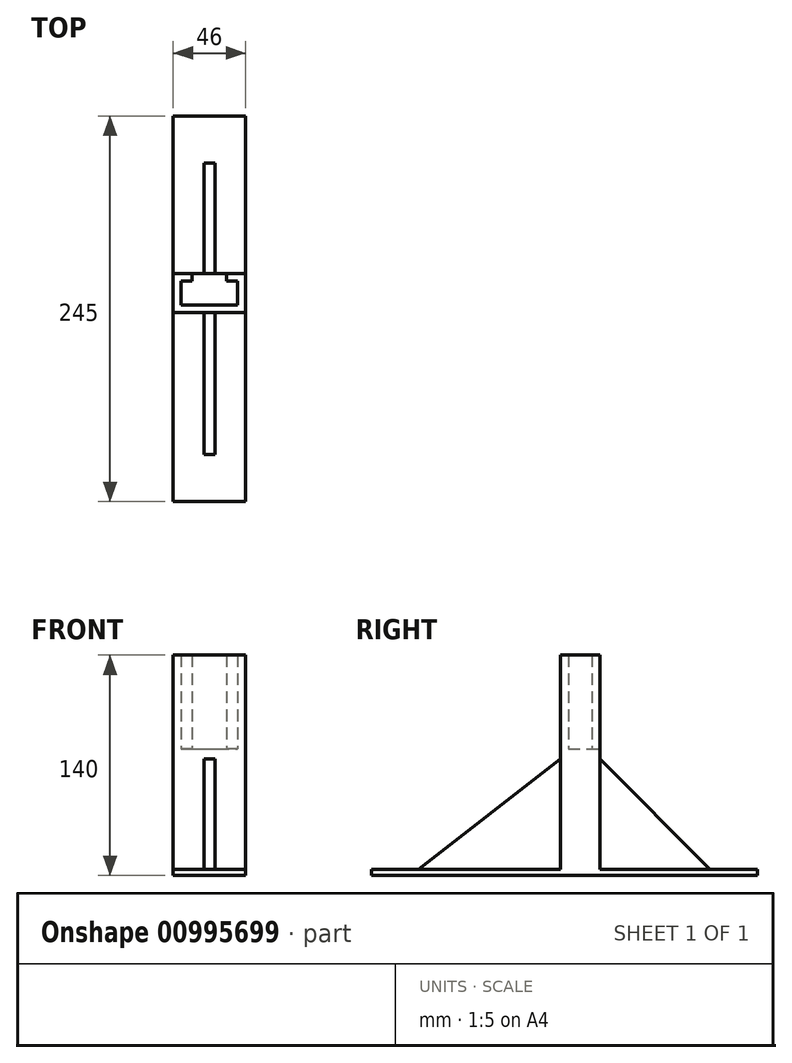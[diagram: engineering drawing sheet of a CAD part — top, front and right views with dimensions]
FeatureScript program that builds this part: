
annotation { "Feature Type Name" : "Feature", "Feature Type Description" : "" }
export const myFeature = defineFeature(function(context is Context, id is Id, definition is map)
    precondition{}
    {
        {
            var Q0;
            Q0=qCreatedBy(makeId("Front.planeOp"),FACE);
            var sketch = newSketch(context, id + "F0", { "sketchPlane" : qUnion([Q0])});
            skLineSegment(sketch, "E0.bottom", {"start": v(-35.47, 8.44) * mm, "end": v(10.53, 8.44) * mm});
            skLineSegment(sketch, "E0.top", {"start": v(-35.47, -71.56) * mm, "end": v(10.53, -71.56) * mm});
            skLineSegment(sketch, "E0.left", {"start": v(-35.47, 8.44) * mm, "end": v(-35.47, -71.56) * mm});
            skLineSegment(sketch, "E0.right", {"start": v(10.53, 8.44) * mm, "end": v(10.53, -71.56) * mm});
            skSolve(sketch);
        }
        {
            var Q0;
            Q0=makeQuery(id+"F0.imprint","IMPRINT",FACE,{"disambiguationData":[TD([[makeQuery(id+"F0.imprint","IMPRINT",EDGE,{"derivedFrom":sQuery(id+"F0.wireOp",EDGE,"E0.bottom")}),-1.0]])]});
            extrude(context, id + "F1", {"entities" : qUnion([Q0]), "depth" : 25 * mm, "offsetDistance" : 25 * mm});
        }
        {
            var Q0;
            Q0=makeQuery(id+"F1.opExtrude","SWEPT_FACE",FACE,{"disambiguationData":[OSD([sQuery(id+"F0.wireOp",EDGE,"E0.left")])]});
            var sketch = newSketch(context, id + "F2", { "sketchPlane" : qUnion([Q0])});
            skLineSegment(sketch, "E1", {"start": v(0, -71.56) * mm, "end": v(-100, -71.56) * mm});
            skLineSegment(sketch, "E2", {"start": v(-100, -71.56) * mm, "end": v(-100, -67.56) * mm});
            skLineSegment(sketch, "E3", {"start": v(-100, -67.56) * mm, "end": v(0, -67.56) * mm});
            skLineSegment(sketch, "E4", {"start": v(-70, -67.56) * mm, "end": v(0, 2.44) * mm});
            skLineSegment(sketch, "E5", {"start": v(25, -71.56) * mm, "end": v(145, -71.56) * mm});
            skLineSegment(sketch, "E6", {"start": v(145, -71.56) * mm, "end": v(145, -67.56) * mm});
            skLineSegment(sketch, "E7", {"start": v(145, -67.56) * mm, "end": v(25, -67.56) * mm});
            skLineSegment(sketch, "E8", {"start": v(25, 2.44) * mm, "end": v(115, -67.56) * mm});
            skSolve(sketch);
        }
        {
            var Q0;
            Q0=makeQuery(id+"F1.opExtrude","SWEPT_FACE",FACE,{"disambiguationData":[OSD([sQuery(id+"F0.wireOp",EDGE,"E0.bottom")])]});
            var sketch = newSketch(context, id + "F3", { "sketchPlane" : qUnion([Q0])});
            skLineSegment(sketch, "E9.0.0", {"start": v(10.53, 0) * mm, "end": v(-35.47, 0) * mm});
            skLineSegment(sketch, "E9.0.1", {"start": v(-35.47, 0) * mm, "end": v(-35.47, -25) * mm});
            skLineSegment(sketch, "E9.0.2", {"start": v(-35.47, -25) * mm, "end": v(10.53, -25) * mm});
            skLineSegment(sketch, "E9.0.3", {"start": v(10.53, -25) * mm, "end": v(10.53, 0) * mm});
            skLineSegment(sketch, "E10.0", {"start": v(5.53, -5) * mm, "end": v(-1.47, -5) * mm});
            skLineSegment(sketch, "E10.1", {"start": v(5.53, -20) * mm, "end": v(5.53, -5) * mm});
            skLineSegment(sketch, "E10.2", {"start": v(-30.47, -20) * mm, "end": v(5.53, -20) * mm});
            skLineSegment(sketch, "E10.3", {"start": v(-30.47, -5) * mm, "end": v(-30.47, -20) * mm});
            skLineSegment(sketch, "E11", {"start": v(-1.47, -5) * mm, "end": v(-23.47, -5) * mm});
            skLineSegment(sketch, "E12", {"start": v(-23.47, -5) * mm, "end": v(-30.47, -5) * mm});
            skLineSegment(sketch, "E13", {"start": v(-1.47, -5) * mm, "end": v(-1.47, 0) * mm});
            skLineSegment(sketch, "E14", {"start": v(-23.47, -5) * mm, "end": v(-23.47, 0) * mm});
            skSolve(sketch);
        }
        {
            var Q0;
            {var subQ6=sQuery(id+"F3.wireOp",EDGE,"E9.0.1");Q0=makeQuery(id+"F3.imprint","IMPRINT",FACE,{"disambiguationData":[TD([[makeQuery(id+"F3.imprint","IMPRINT",EDGE,{"derivedFrom":subQ6}),-1.0]])]});}
            extrude(context, id + "F4", {"entities" : qUnion([Q0]), "operationType" : NewBodyOperationType.ADD, "depth" : 60 * mm, "offsetDistance" : 25 * mm});
        }
        {
            var Q0;
            {var subQ6=sQuery(id+"F2.wireOp",EDGE,"E1");Q0=makeQuery(id+"F2.imprint","IMPRINT",FACE,{"disambiguationData":[TD([[makeQuery(id+"F2.imprint","IMPRINT",EDGE,{"derivedFrom":subQ6}),-1.0]])]});}
            var Q1;
            {var subQ6=sQuery(id+"F2.wireOp",EDGE,"E5");Q1=makeQuery(id+"F2.imprint","IMPRINT",FACE,{"disambiguationData":[TD([[makeQuery(id+"F2.imprint","IMPRINT",EDGE,{"derivedFrom":subQ6}),1.0]])]});}
            extrude(context, id + "F5", {"entities" : qUnion([Q0, Q1]), "operationType" : NewBodyOperationType.ADD, "oppositeDirection" : true, "depth" : 46 * mm, "offsetDistance" : 25 * mm});
        }
        {
            var Q0;
            {var subQ0=sQuery(id+"F0.wireOp",EDGE,"E0.left");Q0=makeQuery(id+"F5.boolean.opBoolean","MERGE",FACE,{"derivedFrom":[makeQuery(id+"F4.boolean.opBoolean","MERGE",FACE,{"derivedFrom":[makeQuery(id+"F1.opExtrude","SWEPT_FACE",FACE,{"disambiguationData":[OSD([subQ0])]}),makeQuery(id+"F4.opExtrude","SWEPT_FACE",FACE,{"disambiguationData":[OSD([sQuery(id+"F3.wireOp",EDGE,"E9.0.1")])]})]}),makeQuery(id+"F5.opExtrude","CAP_FACE",FACE,{"disambiguationData":[OSD([subQ0,sQuery(id+"F2.wireOp",EDGE,"E1"),sQuery(id+"F2.wireOp",EDGE,"E2"),sQuery(id+"F2.wireOp",EDGE,"E3")])],"isStart":true}),makeQuery(id+"F5.opExtrude","CAP_FACE",FACE,{"disambiguationData":[OSD([subQ0,sQuery(id+"F2.wireOp",EDGE,"E5"),sQuery(id+"F2.wireOp",EDGE,"E6"),sQuery(id+"F2.wireOp",EDGE,"E7")])],"isStart":true})]});}
            cPlane(context, id + "F6", {"entities" : qUnion([Q0]), "cplaneType" : CPlaneType.OFFSET, "offset" : 23 * mm, "oppositeDirection" : true, "width" : 150 * mm, "height" : 150 * mm});
        }
        {
            var Q0;
            Q0=qCreatedBy(id+"F6.planeOp",FACE);
            var sketch = newSketch(context, id + "F7", { "sketchPlane" : qUnion([Q0])});
            skLineSegment(sketch, "E15.0.0", {"start": v(0, 68.44) * mm, "end": v(0, -67.56) * mm});
            skLineSegment(sketch, "E15.0.2", {"start": v(0, -67.56) * mm, "end": v(0, 68.44) * mm});
            skLineSegment(sketch, "E15.0.4", {"start": v(0, 8.44) * mm, "end": v(0, 68.44) * mm});
            skLineSegment(sketch, "E15.0.6", {"start": v(0, 8.44) * mm, "end": v(0, 68.44) * mm});
            skLineSegment(sketch, "E16", {"start": v(0, -67.56) * mm, "end": v(-70, -67.56) * mm});
            skLineSegment(sketch, "E17", {"start": v(-70, -67.56) * mm, "end": v(0, 2.44) * mm});
            skLineSegment(sketch, "E18.0.1", {"start": v(25, -67.56) * mm, "end": v(25, 68.44) * mm});
            skLineSegment(sketch, "E18.0.3", {"start": v(25, 68.44) * mm, "end": v(25, -67.56) * mm});
            skLineSegment(sketch, "E19", {"start": v(25, -67.56) * mm, "end": v(115, -67.56) * mm});
            skLineSegment(sketch, "E20", {"start": v(115, -67.56) * mm, "end": v(25, 2.44) * mm});
            skSolve(sketch);
        }
        {
            var Q0;
            {var subQ0=sQuery(id+"F7.wireOp",EDGE,"E16");Q0=makeQuery(id+"F7.imprint","IMPRINT",FACE,{"disambiguationData":[TD([[makeQuery(id+"F7.imprint","IMPRINT",EDGE,{"derivedFrom":subQ0}),-1.0]])]});}
            var Q1;
            {var subQ0=sQuery(id+"F7.wireOp",EDGE,"E19");Q1=makeQuery(id+"F7.imprint","IMPRINT",FACE,{"disambiguationData":[TD([[makeQuery(id+"F7.imprint","IMPRINT",EDGE,{"derivedFrom":subQ0}),1.0]])]});}
            extrude(context, id + "F8", {"entities" : qUnion([Q0, Q1]), "operationType" : NewBodyOperationType.ADD, "endBound" : BoundingType.SYMMETRIC, "depth" : 7 * mm, "offsetDistance" : 25 * mm});
        }
        {
            var Q0;
            {var subQ0=sQuery(id+"F3.wireOp",EDGE,"E9.0.0");Q0=makeQuery(id+"F4.boolean.opBoolean","MERGE",FACE,{"derivedFrom":[makeQuery(id+"F1.opExtrude","CAP_FACE",FACE,{"disambiguationData":[OSD([sQuery(id+"F0.wireOp",EDGE,"E0.bottom"),sQuery(id+"F0.wireOp",EDGE,"E0.top"),sQuery(id+"F0.wireOp",EDGE,"E0.left"),sQuery(id+"F0.wireOp",EDGE,"E0.right")])],"isStart":true}),makeQuery(id+"F4.opExtrude","SWEPT_FACE",FACE,{"disambiguationData":[OSD([subQ0]),TDD([makeQuery(id+"F3.imprint","IMPRINT",EDGE,{"disambiguationData":[TD([[makeQuery(id+"F3.imprint","INTERSECT",VERTEX,{"derivedFrom":[subQ0,sQuery(id+"F3.wireOp",EDGE,"E9.0.1")]}),-1.0]])],"derivedFrom":subQ0})])]}),makeQuery(id+"F4.opExtrude","SWEPT_FACE",FACE,{"disambiguationData":[OSD([subQ0]),TDD([makeQuery(id+"F3.imprint","IMPRINT",EDGE,{"disambiguationData":[TD([[makeQuery(id+"F3.imprint","INTERSECT",VERTEX,{"derivedFrom":[subQ0,sQuery(id+"F3.wireOp",EDGE,"E9.0.3")]}),1.0]])],"derivedFrom":subQ0})])]})]});}
            var sketch = newSketch(context, id + "F9", { "sketchPlane" : qUnion([Q0])});
            skLineSegment(sketch, "E21", {"start": v(21.72, 8.84) * mm, "end": v(21.72, -71.56) * mm});
            skSolve(sketch);
        }
        {
            var Q0;
            Q0=makeQuery(id+"F1.opExtrude","SWEPT_FACE",FACE,{"disambiguationData":[OSD([sQuery(id+"F0.wireOp",EDGE,"E0.bottom")])]});
            var Q1;
            Q1=sQuery(id+"F9.wireOp",VERTEX,"E21.start");
            extrude(context, id + "F10", {"entities" : qUnion([Q0]), "operationType" : NewBodyOperationType.ADD, "endBound" : BoundingType.UP_TO_VERTEX, "depth" : 2.2 * mm, "endBoundEntityVertex" : qUnion([Q1]), "offsetDistance" : 25 * mm});
        }
    });
